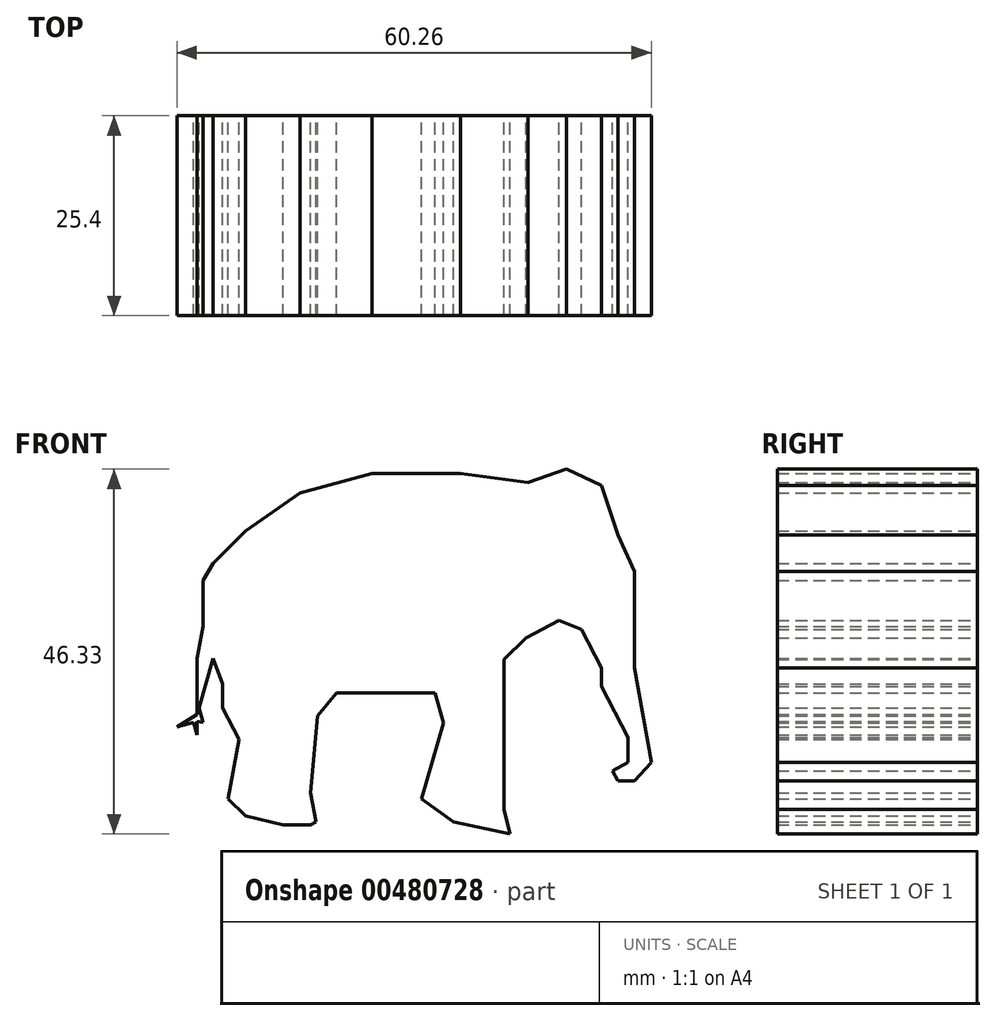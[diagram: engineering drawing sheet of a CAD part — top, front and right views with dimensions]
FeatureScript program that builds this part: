
annotation { "Feature Type Name" : "Feature", "Feature Type Description" : "" }
export const myFeature = defineFeature(function(context is Context, id is Id, definition is map)
    precondition{}
    {
        {
            var Q0;
            Q0=qCreatedBy(makeId("Front.planeOp"),FACE);
            var sketch = newSketch(context, id + "F0", { "sketchPlane" : qUnion([Q0])});
            skLineSegment(sketch, "E0", {"start": v(14.78, 23.54) * mm, "end": v(19.69, 25.24) * mm});
            skLineSegment(sketch, "E1", {"start": v(19.69, 25.24) * mm, "end": v(24.12, 23.17) * mm});
            skLineSegment(sketch, "E2", {"start": v(24.12, 23.17) * mm, "end": v(26.2, 16.84) * mm});
            skLineSegment(sketch, "E3", {"start": v(26.2, 16.84) * mm, "end": v(28.27, 12.22) * mm});
            skLineSegment(sketch, "E4", {"start": v(28.27, 12.22) * mm, "end": v(28.27, 4.86) * mm});
            skLineSegment(sketch, "E5", {"start": v(28.27, 4.86) * mm, "end": v(29.7, 3.07) * mm});
            skLineSegment(sketch, "E6", {"start": v(29.7, 3.07) * mm, "end": v(31.67, 3.07) * mm});
            skLineSegment(sketch, "E7", {"start": v(31.67, 3.07) * mm, "end": v(32.33, 3.07) * mm});
            skLineSegment(sketch, "E8", {"start": v(32.33, 3.07) * mm, "end": v(30.45, 1.09) * mm});
            skLineSegment(sketch, "E9", {"start": v(30.45, 1.09) * mm, "end": v(28.27, 1.84) * mm});
            skLineSegment(sketch, "E10", {"start": v(28.27, 1.84) * mm, "end": v(28.27, 0) * mm});
            skLineSegment(sketch, "E11", {"start": v(28.27, 0) * mm, "end": v(29.6, -1.08) * mm});
            skLineSegment(sketch, "E12", {"start": v(29.6, -1.08) * mm, "end": v(31.67, 0) * mm});
            skLineSegment(sketch, "E13", {"start": v(31.67, 0) * mm, "end": v(30.45, 1.09) * mm});
            skLineSegment(sketch, "E14", {"start": v(28.27, 1.84) * mm, "end": v(28.27, 4.86) * mm});
            skLineSegment(sketch, "E15", {"start": v(28.27, 0) * mm, "end": v(30.45, -12.03) * mm});
            skLineSegment(sketch, "E16", {"start": v(30.45, -12.03) * mm, "end": v(28.27, -14.39) * mm});
            skLineSegment(sketch, "E17", {"start": v(28.27, -14.39) * mm, "end": v(26.2, -14.39) * mm});
            skLineSegment(sketch, "E18", {"start": v(26.2, -14.39) * mm, "end": v(25.51, -13.07) * mm});
            skLineSegment(sketch, "E19", {"start": v(25.51, -13.07) * mm, "end": v(27.51, -12.03) * mm});
            skLineSegment(sketch, "E20", {"start": v(27.51, -12.03) * mm, "end": v(27.51, -8.82) * mm});
            skLineSegment(sketch, "E21", {"start": v(27.51, -8.82) * mm, "end": v(26.67, -7.21) * mm});
            skLineSegment(sketch, "E22", {"start": v(26.67, -7.21) * mm, "end": v(25.51, -5) * mm});
            skLineSegment(sketch, "E23", {"start": v(25.51, -5) * mm, "end": v(24.12, -2.34) * mm});
            skLineSegment(sketch, "E24", {"start": v(24.12, -2.34) * mm, "end": v(24.12, 0) * mm});
            skLineSegment(sketch, "E25", {"start": v(24.12, 0) * mm, "end": v(22.52, 3.07) * mm});
            skLineSegment(sketch, "E26", {"start": v(22.52, 3.07) * mm, "end": v(21.58, 4.86) * mm});
            skLineSegment(sketch, "E27", {"start": v(21.58, 4.86) * mm, "end": v(18.74, 6) * mm});
            skLineSegment(sketch, "E28", {"start": v(18.74, 6) * mm, "end": v(17.15, 5.16) * mm});
            skLineSegment(sketch, "E29", {"start": v(17.15, 5.16) * mm, "end": v(14.53, 3.8) * mm});
            skLineSegment(sketch, "E30", {"start": v(14.53, 3.8) * mm, "end": v(11.76, 1.09) * mm});
            skLineSegment(sketch, "E31", {"start": v(11.76, 1.09) * mm, "end": v(11.76, -16.65) * mm});
            skLineSegment(sketch, "E32", {"start": v(11.76, -16.65) * mm, "end": v(11.76, -17.98) * mm});
            skLineSegment(sketch, "E33", {"start": v(11.76, -17.98) * mm, "end": v(12.52, -21.09) * mm});
            skLineSegment(sketch, "E34", {"start": v(12.52, -21.09) * mm, "end": v(5.34, -19.58) * mm});
            skLineSegment(sketch, "E35", {"start": v(5.34, -19.58) * mm, "end": v(1.29, -16.65) * mm});
            skLineSegment(sketch, "E36", {"start": v(1.29, -16.65) * mm, "end": v(4.02, -7.03) * mm});
            skLineSegment(sketch, "E37", {"start": v(4.02, -7.03) * mm, "end": v(2.99, -3.16) * mm});
            skLineSegment(sketch, "E38", {"start": v(2.99, -3.16) * mm, "end": v(-9.56, -3.16) * mm});
            skLineSegment(sketch, "E39", {"start": v(-9.56, -3.16) * mm, "end": v(-11.92, -6.09) * mm});
            skLineSegment(sketch, "E40", {"start": v(-11.92, -6.09) * mm, "end": v(-12.87, -15.9) * mm});
            skLineSegment(sketch, "E41", {"start": v(-12.87, -15.9) * mm, "end": v(-12.11, -19.58) * mm});
            skLineSegment(sketch, "E42", {"start": v(-12.11, -19.58) * mm, "end": v(-12.87, -19.97) * mm});
            skLineSegment(sketch, "E43", {"start": v(-12.87, -19.97) * mm, "end": v(-16.36, -19.97) * mm});
            skLineSegment(sketch, "E44", {"start": v(-16.36, -19.97) * mm, "end": v(-21.08, -18.82) * mm});
            skLineSegment(sketch, "E45", {"start": v(-21.08, -18.82) * mm, "end": v(-23.34, -16.65) * mm});
            skLineSegment(sketch, "E46", {"start": v(-23.34, -16.65) * mm, "end": v(-21.93, -9.1) * mm});
            skLineSegment(sketch, "E47", {"start": v(-21.93, -9.1) * mm, "end": v(-24.04, -5.06) * mm});
            skLineSegment(sketch, "E48", {"start": v(-24.04, -5.06) * mm, "end": v(-24.04, -2.03) * mm});
            skLineSegment(sketch, "E49", {"start": v(-24.04, -2.03) * mm, "end": v(-25.23, 1.18) * mm});
            skLineSegment(sketch, "E50", {"start": v(-25.23, 1.18) * mm, "end": v(-27.02, -5.06) * mm});
            skLineSegment(sketch, "E51", {"start": v(-27.02, -5.06) * mm, "end": v(-26.36, -7.5) * mm});
            skLineSegment(sketch, "E52", {"start": v(-26.36, -7.5) * mm, "end": v(-26.51, -6.93) * mm});
            skLineSegment(sketch, "E53", {"start": v(-26.51, -6.93) * mm, "end": v(-27.28, -6.8) * mm});
            skLineSegment(sketch, "E54", {"start": v(-27.28, -6.8) * mm, "end": v(-27.28, -8.54) * mm});
            skLineSegment(sketch, "E55", {"start": v(-27.28, -8.54) * mm, "end": v(-27.72, -6.93) * mm});
            skLineSegment(sketch, "E56", {"start": v(-27.72, -6.93) * mm, "end": v(-29.8, -7.5) * mm});
            skLineSegment(sketch, "E57", {"start": v(-29.8, -7.5) * mm, "end": v(-27.28, -5.9) * mm});
            skLineSegment(sketch, "E58", {"start": v(-27.28, -5.9) * mm, "end": v(-27.28, 1.18) * mm});
            skLineSegment(sketch, "E59", {"start": v(-27.28, 1.18) * mm, "end": v(-26.51, 5.28) * mm});
            skLineSegment(sketch, "E60", {"start": v(-26.51, 5.28) * mm, "end": v(-26.51, 11.09) * mm});
            skLineSegment(sketch, "E61", {"start": v(-26.51, 11.09) * mm, "end": v(-25.23, 13.26) * mm});
            skLineSegment(sketch, "E62", {"start": v(-25.23, 13.26) * mm, "end": v(-21.08, 17.41) * mm});
            skLineSegment(sketch, "E63", {"start": v(-21.08, 17.41) * mm, "end": v(-14.19, 22.22) * mm});
            skLineSegment(sketch, "E64", {"start": v(-14.19, 22.22) * mm, "end": v(-5.05, 24.7) * mm});
            skLineSegment(sketch, "E65", {"start": v(-5.05, 24.7) * mm, "end": v(6.2, 24.7) * mm});
            skLineSegment(sketch, "E66", {"start": v(6.2, 24.7) * mm, "end": v(14.78, 23.54) * mm});
            skSolve(sketch);
        }
        {
            var Q0;
            Q0=makeQuery(id+"F0.imprint","IMPRINT",FACE,{"disambiguationData":[TD([[makeQuery(id+"F0.imprint","IMPRINT",EDGE,{"derivedFrom":sQuery(id+"F0.wireOp",EDGE,"E0")}),-1.0]])]});
            extrude(context, id + "F1", {"entities" : qUnion([Q0]), "depth" : 25.4 * mm});
        }
    });
